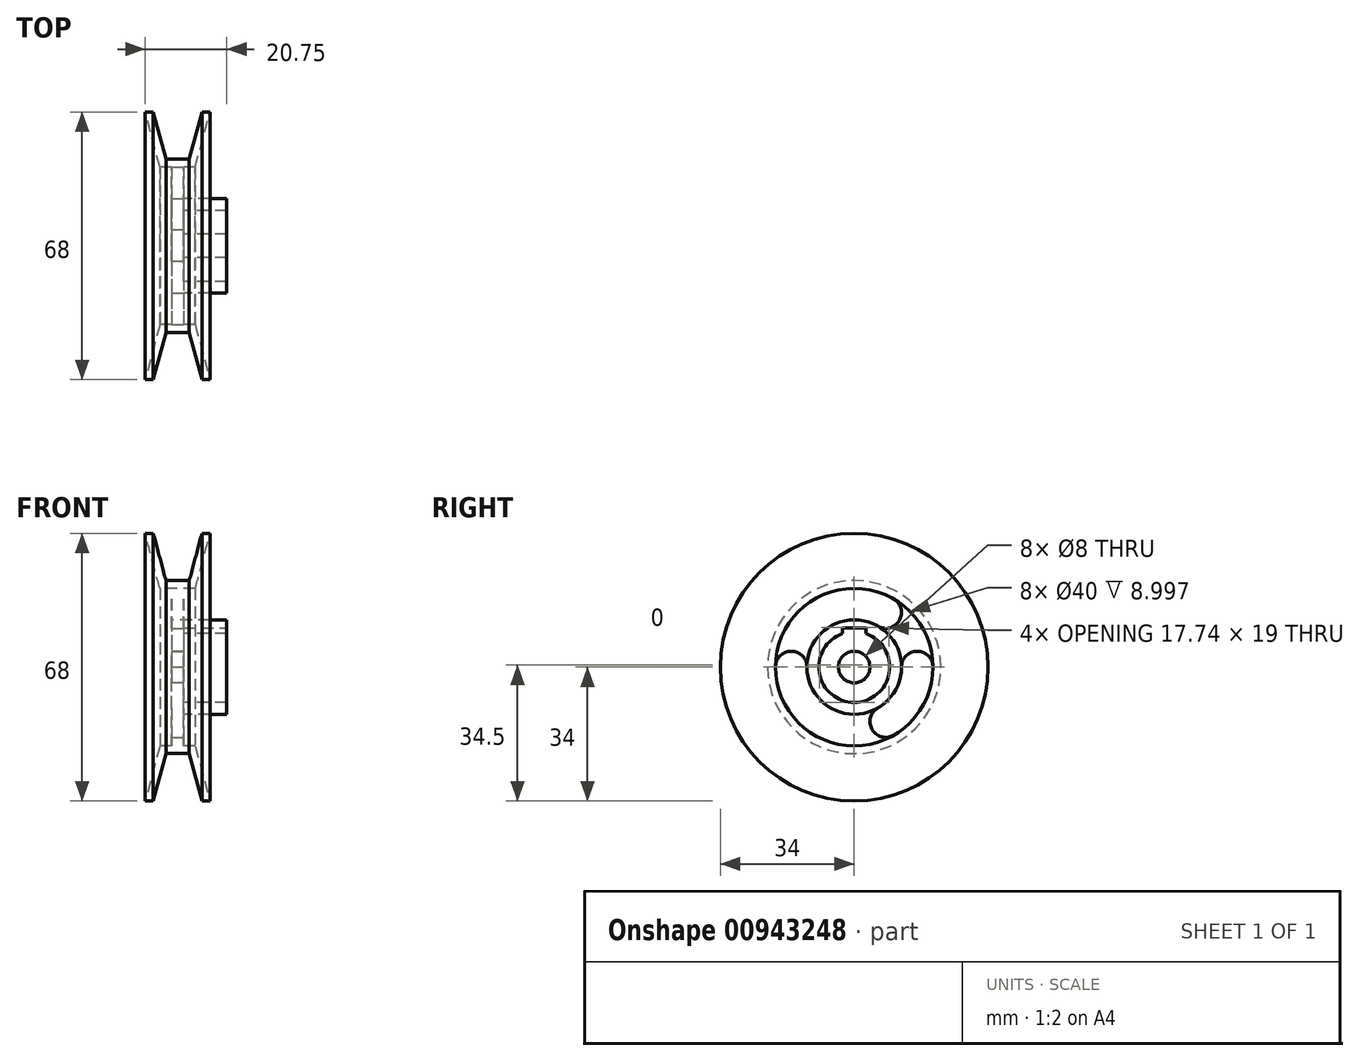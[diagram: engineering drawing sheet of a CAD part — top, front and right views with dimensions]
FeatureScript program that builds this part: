
annotation { "Feature Type Name" : "Feature", "Feature Type Description" : "" }
export const myFeature = defineFeature(function(context is Context, id is Id, definition is map)
    precondition{}
    {
        {
            var Q0;
            Q0=qCreatedBy(makeId("Front.planeOp"),FACE);
            var sketch = newSketch(context, id + "F0", { "sketchPlane" : qUnion([Q0])});
            skLineSegment(sketch, "E0", {"start": v(6.18, 34) * mm, "end": v(8.25, 34) * mm});
            skLineSegment(sketch, "E1", {"start": v(6.18, 34) * mm, "end": v(2.96, 22) * mm});
            skLineSegment(sketch, "E2", {"start": v(8.25, 34) * mm, "end": v(4.5, 20) * mm});
            skLineSegment(sketch, "E3", {"start": v(2.96, 22) * mm, "end": v(0, 22) * mm});
            skLineSegment(sketch, "E4", {"start": v(4.5, 20) * mm, "end": v(1.5, 20) * mm});
            skLineSegment(sketch, "E5", {"start": v(1.5, 20) * mm, "end": v(1.5, 12) * mm});
            skLineSegment(sketch, "E6.MirrorCS", {"start": v(-4.5, 20) * mm, "end": v(-1.5, 20) * mm});
            skLineSegment(sketch, "E7.MirrorCS", {"start": v(-1.5, 20) * mm, "end": v(-1.5, 4) * mm});
            skLineSegment(sketch, "E8.MirrorCS", {"start": v(-8.25, 34) * mm, "end": v(-4.5, 20) * mm});
            skLineSegment(sketch, "E9.MirrorCS", {"start": v(-6.18, 34) * mm, "end": v(-2.96, 22) * mm});
            skLineSegment(sketch, "E10.MirrorCS", {"start": v(-6.18, 34) * mm, "end": v(-8.25, 34) * mm});
            skLineSegment(sketch, "E11.MirrorCS", {"start": v(-2.96, 22) * mm, "end": v(0, 22) * mm});
            skLineSegment(sketch, "E12", {"start": v(-1.5, 4) * mm, "end": v(1.5, 4) * mm});
            skLineSegment(sketch, "E13", {"start": v(-22.44, 0) * mm, "end": v(29.6, 0) * mm, "construction": true});
            skLineSegment(sketch, "E14", {"start": v(1.5, 12) * mm, "end": v(12.5, 12) * mm});
            skLineSegment(sketch, "E15", {"start": v(12.5, 12) * mm, "end": v(12.5, 9) * mm});
            skLineSegment(sketch, "E16", {"start": v(12.5, 9) * mm, "end": v(1.5, 9) * mm});
            skLineSegment(sketch, "E17.trimOffspring", {"start": v(1.5, 9) * mm, "end": v(1.5, 4) * mm});
            skSolve(sketch);
        }
        {
            var Q0;
            Q0=qSketchRegion(id+"F0",true);
            var Q1;
            Q1=sQuery(id+"F0.wireOp",EDGE,"E13");
            revolve(context, id + "F1", {"surfaceOperationType" : NewSurfaceOperationType.NEW, "entities" : qUnion([Q0]), "axis" : qUnion([Q1]), "revolveType" : RevolveType.FULL});
        }
        {
            var Q0;
            Q0=makeQuery(id+"F1.opRevolve","SWEPT_FACE",FACE,{"disambiguationData":[OSD([sQuery(id+"F0.wireOp",EDGE,"E15")])]});
            var sketch = newSketch(context, id + "F2", { "sketchPlane" : qUnion([Q0])});
            skLineSegment(sketch, "E18.bottom", {"start": v(3, 10) * mm, "end": v(-3, 10) * mm});
            skLineSegment(sketch, "E18.top", {"start": v(3, 8) * mm, "end": v(-3, 8) * mm});
            skLineSegment(sketch, "E18.left", {"start": v(3, 10) * mm, "end": v(3, 8) * mm});
            skLineSegment(sketch, "E18.right", {"start": v(-3, 10) * mm, "end": v(-3, 8) * mm});
            skPoint(sketch, "E18.middle", {"position": v(0, 9) * mm});
            skSolve(sketch);
        }
        {
            var Q0;
            Q0=qSketchRegion(id+"F2",true);
            extrude(context, id + "F3", {"entities" : qUnion([Q0]), "operationType" : NewBodyOperationType.REMOVE, "oppositeDirection" : true, "depth" : 11 * mm, "offsetDistance" : 25 * mm});
        }
        {
            var Q0;
            Q0=makeQuery(id+"F1.opRevolve","SWEPT_FACE",FACE,{"disambiguationData":[OSD([sQuery(id+"F0.wireOp",EDGE,"E5")])]});
            var sketch = newSketch(context, id + "F4", { "sketchPlane" : qUnion([Q0])});
            skArc(sketch, "E19", {"start": v(-16, 0) * mm, "mid": v(-13.86, -8) * mm, "end": v(-8, -13.86) * mm});
            skLineSegment(sketch, "E20", {"start": v(-8, -13.86) * mm, "end": v(0, 0) * mm, "construction": true});
            skArc(sketch, "E21.0.startCap", {"start": v(-20, 0) * mm, "mid": v(-16, 4) * mm, "end": v(-12, 0) * mm});
            skArc(sketch, "E21.0.endCap", {"start": v(-6, -10.4) * mm, "mid": v(-4.54, -15.86) * mm, "end": v(-10, -17.32) * mm});
            skArc(sketch, "E21.0.left", {"start": v(-12, 0) * mm, "mid": v(-10.4, -6) * mm, "end": v(-6, -10.4) * mm});
            skArc(sketch, "E21.0.right", {"start": v(-20, 0) * mm, "mid": v(-17.32, -10) * mm, "end": v(-10, -17.32) * mm});
            skArc(sketch, "E22.1.0", {"start": v(8, -13.86) * mm, "mid": v(13.86, -8) * mm, "end": v(16, 0) * mm});
            skArc(sketch, "E22.1.1", {"start": v(10, -17.32) * mm, "mid": v(17.32, -10) * mm, "end": v(20, 0) * mm});
            skArc(sketch, "E22.1.2", {"start": v(6, -10.4) * mm, "mid": v(10.4, -6) * mm, "end": v(12, 0) * mm});
            skArc(sketch, "E22.1.3", {"start": v(12, 0) * mm, "mid": v(16, 4) * mm, "end": v(20, 0) * mm});
            skArc(sketch, "E22.1.4", {"start": v(10, -17.32) * mm, "mid": v(4.54, -15.86) * mm, "end": v(6, -10.4) * mm});
            skArc(sketch, "E22.2.0", {"start": v(8, 13.86) * mm, "mid": v(0, 16) * mm, "end": v(-8, 13.86) * mm});
            skArc(sketch, "E22.2.1", {"start": v(10, 17.32) * mm, "mid": v(0, 20) * mm, "end": v(-10, 17.32) * mm});
            skArc(sketch, "E22.2.2", {"start": v(6, 10.4) * mm, "mid": v(0, 12) * mm, "end": v(-6, 10.4) * mm});
            skArc(sketch, "E22.2.3", {"start": v(-6, 10.4) * mm, "mid": v(-11.46, 11.86) * mm, "end": v(-10, 17.32) * mm});
            skArc(sketch, "E22.2.4", {"start": v(10, 17.32) * mm, "mid": v(11.46, 11.86) * mm, "end": v(6, 10.4) * mm});
            skSolve(sketch);
        }
        {
            var Q0;
            Q0=makeQuery(id+"F4.imprint","IMPRINT",FACE,{"disambiguationData":[TD([[makeQuery(id+"F4.imprint","IMPRINT",EDGE,{"derivedFrom":sQuery(id+"F4.wireOp",EDGE,"E21.0.startCap")}),-1.0]])]});
            var Q1;
            Q1=makeQuery(id+"F4.imprint","IMPRINT",FACE,{"disambiguationData":[TD([[makeQuery(id+"F4.imprint","IMPRINT",EDGE,{"derivedFrom":sQuery(id+"F4.wireOp",EDGE,"E22.2.1")}),-1.0]])]});
            var Q2;
            Q2=makeQuery(id+"F4.imprint","IMPRINT",FACE,{"disambiguationData":[TD([[makeQuery(id+"F4.imprint","IMPRINT",EDGE,{"derivedFrom":sQuery(id+"F4.wireOp",EDGE,"E22.1.1")}),-1.0]])]});
            extrude(context, id + "F5", {"entities" : qUnion([Q0, Q1, Q2]), "operationType" : NewBodyOperationType.REMOVE, "oppositeDirection" : true, "depth" : 25 * mm, "offsetDistance" : 25 * mm});
        }
    });
